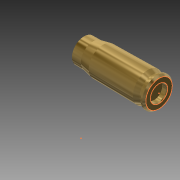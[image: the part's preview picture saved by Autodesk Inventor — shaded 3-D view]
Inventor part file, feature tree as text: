
AUTODESK INVENTOR PART (.ipt)
format: ipt  version: 2011 SP1 (Build 150282100, 282)  size: 730,624 bytes
history: native  units: mm
features: sketch x6, extrude x5, other x1, revolve x1, shell x1
ambient origin geometry x8: Origin, YZ Plane, XZ Plane, XY Plane, X Axis, Y Axis, Z Axis, Center Point
feature tree (14):
  other  "Твердое тело1"
  revolve  "Вращение1"
  extrude  "Выдавливание1"  TaperAngle=90.0deg  [1 undecoded]
  extrude  "Выдавливание2"  Depth=18.601302mm
  shell  "Оболочка1"  Thickness=45.0mm
  extrude  "Выдавливание3"  Depth=1.25mm TaperAngle=0.0deg
  extrude  "Выдавливание4"  Depth=0.3mm
  extrude  "Выдавливание5"  Depth=0.3mm
  sketch  "Эскиз1"
  sketch  "Эскиз2"
  sketch  "Эскиз3"
  sketch  "Эскиз4"
  sketch  "Эскиз5"
  sketch  "Эскиз6"
note: 1 required parameter value undecoded (feature->parameter linkage not recoverable at this tier; creation-order binding heuristic only, values carry confidence <= 0.55)
